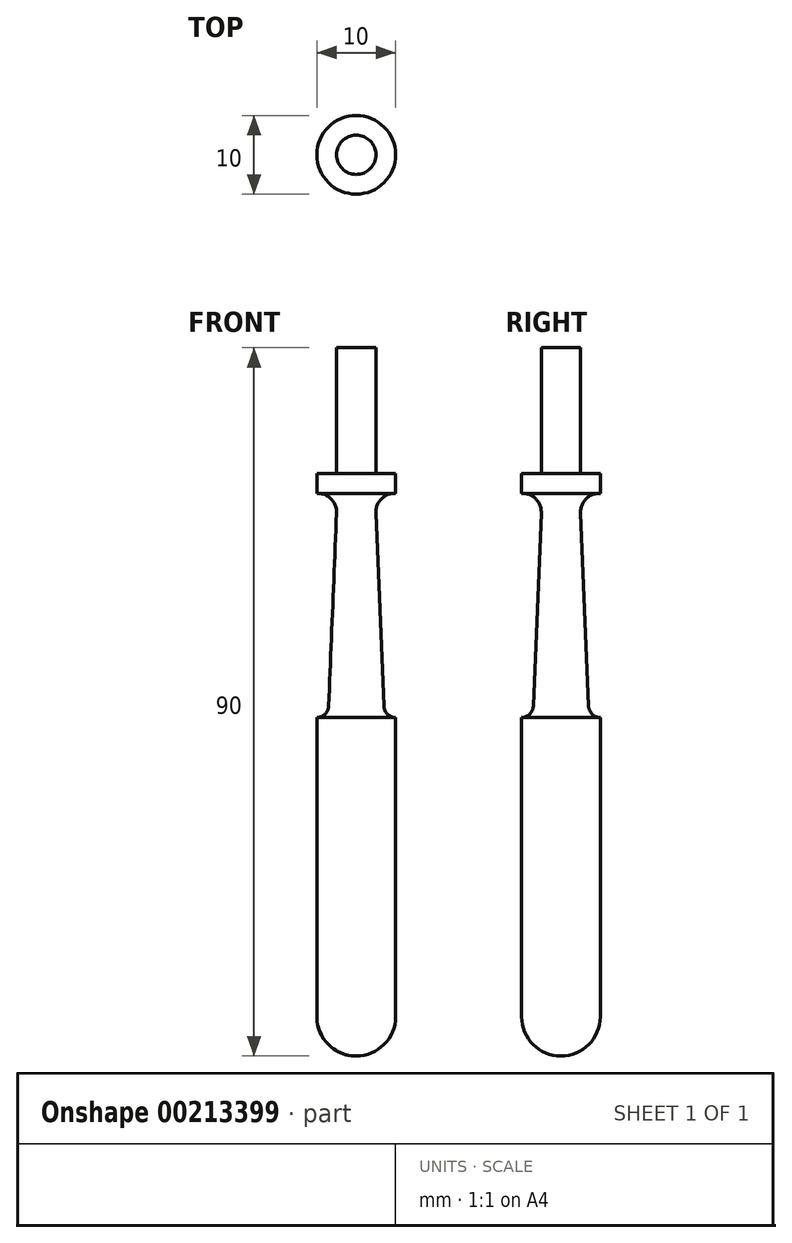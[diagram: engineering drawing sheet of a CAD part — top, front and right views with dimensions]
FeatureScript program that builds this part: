
annotation { "Feature Type Name" : "Feature", "Feature Type Description" : "" }
export const myFeature = defineFeature(function(context is Context, id is Id, definition is map)
    precondition{}
    {
        {
            var Q0;
            Q0=qCreatedBy(makeId("Front.planeOp"),FACE);
            var sketch = newSketch(context, id + "F0", { "sketchPlane" : qUnion([Q0])});
            skLineSegment(sketch, "E0", {"start": v(-48.43, -43.52) * mm, "end": v(-48.43, -5.52) * mm});
            skLineSegment(sketch, "E1", {"start": v(-43.43, -43.52) * mm, "end": v(-43.43, 22.98) * mm});
            skLineSegment(sketch, "E2", {"start": v(-45.93, 20.48) * mm, "end": v(-46.93, -4.02) * mm});
            skArc(sketch, "E3", {"start": v(-45.93, 20.48) * mm, "mid": v(-46.63, 22.28) * mm, "end": v(-48.43, 22.98) * mm});
            skArc(sketch, "E4", {"start": v(-46.93, -4.02) * mm, "mid": v(-47.39, -5.06) * mm, "end": v(-48.43, -5.52) * mm});
            skLineSegment(sketch, "E5", {"start": v(-43.43, -43.52) * mm, "end": v(-43.43, -48.52) * mm});
            skArc(sketch, "E6", {"start": v(-48.43, -43.52) * mm, "mid": v(-46.97, -47.06) * mm, "end": v(-43.43, -48.52) * mm});
            skLineSegment(sketch, "E7", {"start": v(-48.43, 22.98) * mm, "end": v(-48.43, 25.48) * mm});
            skLineSegment(sketch, "E8", {"start": v(-43.43, 25.48) * mm, "end": v(-43.43, 22.98) * mm});
            skLineSegment(sketch, "E9", {"start": v(-45.93, 25.48) * mm, "end": v(-45.93, 41.48) * mm});
            skLineSegment(sketch, "E10", {"start": v(-45.93, 41.48) * mm, "end": v(-43.43, 41.48) * mm});
            skLineSegment(sketch, "E11", {"start": v(-43.43, 41.48) * mm, "end": v(-43.43, 25.48) * mm});
            skLineSegment(sketch, "E12", {"start": v(-48.43, 25.48) * mm, "end": v(-45.93, 25.48) * mm});
            skSolve(sketch);
        }
        {
            var Q0;
            Q0=qSketchRegion(id+"F0",true);
            var Q1;
            Q1=sQuery(id+"F0.wireOp",EDGE,"E1");
            revolve(context, id + "F1", {"entities" : qUnion([Q0]), "axis" : qUnion([Q1]), "revolveType" : RevolveType.FULL});
        }
    });
